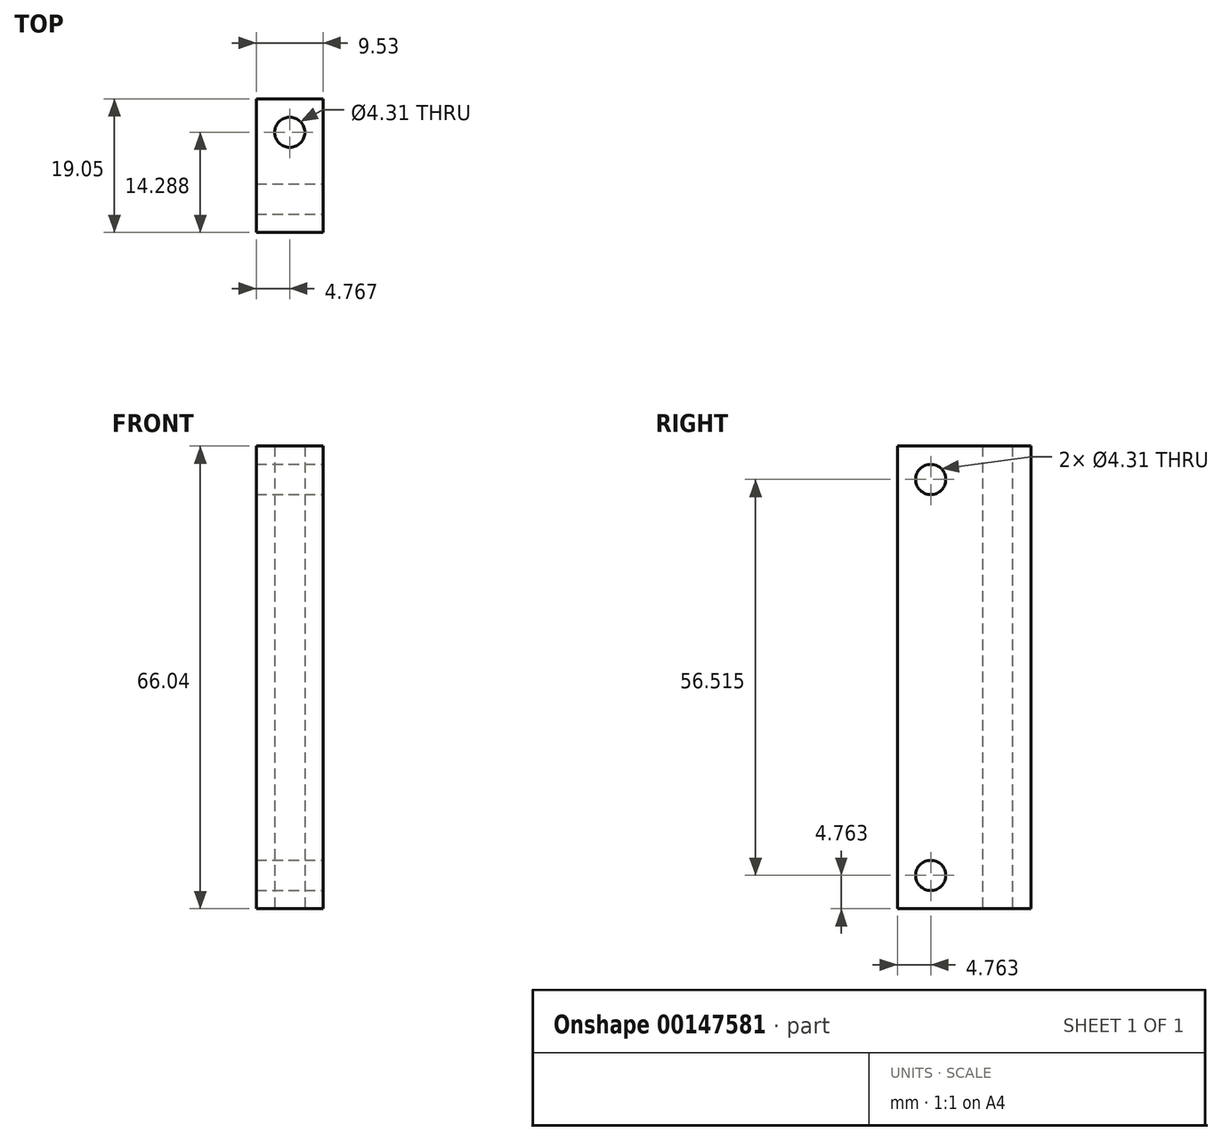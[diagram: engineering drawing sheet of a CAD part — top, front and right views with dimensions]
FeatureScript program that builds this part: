
annotation { "Feature Type Name" : "Feature", "Feature Type Description" : "" }
export const myFeature = defineFeature(function(context is Context, id is Id, definition is map)
    precondition{}
    {
        {
            var Q0;
            Q0=qCreatedBy(makeId("Top.planeOp"),FACE);
            var sketch = newSketch(context, id + "F0", { "sketchPlane" : qUnion([Q0])});
            skLineSegment(sketch, "E0.bottom", {"start": v(0, 0) * mm, "end": v(-9.53, 0) * mm});
            skLineSegment(sketch, "E0.top", {"start": v(0, -19.05) * mm, "end": v(-9.52, -19.05) * mm});
            skLineSegment(sketch, "E0.left", {"start": v(0, 0) * mm, "end": v(0, -19.05) * mm});
            skLineSegment(sketch, "E0.right", {"start": v(-9.52, 0) * mm, "end": v(-9.52, -19.05) * mm});
            skLineSegment(sketch, "E1", {"start": v(-4.76, 0) * mm, "end": v(-4.76, -4.76) * mm, "construction": true});
            skLineSegment(sketch, "E2", {"start": v(-4.76, -4.76) * mm, "end": v(0, -4.76) * mm, "construction": true});
            skCircle(sketch, "E3", {"center": v(-4.76, -4.76) * mm, "radius": 2.15 * mm});
            skSolve(sketch);
        }
        {
            var Q0;
            Q0=qSketchRegion(id+"F0",true);
            extrude(context, id + "F1", {"entities" : qUnion([Q0]), "depth" : 66.04 * mm});
        }
        {
            var Q0;
            Q0=makeQuery(id+"F1.opExtrude","SWEPT_FACE",FACE,{"disambiguationData":[OSD([sQuery(id+"F0.wireOp",EDGE,"E0.left")])]});
            var sketch = newSketch(context, id + "F2", { "sketchPlane" : qUnion([Q0])});
            skLineSegment(sketch, "E4", {"start": v(-14.29, 66.04) * mm, "end": v(-14.29, 61.28) * mm, "construction": true});
            skLineSegment(sketch, "E5", {"start": v(-14.29, 61.28) * mm, "end": v(-19.05, 61.28) * mm, "construction": true});
            skLineSegment(sketch, "E6", {"start": v(-14.29, 0) * mm, "end": v(-14.29, 4.76) * mm, "construction": true});
            skCircle(sketch, "E7", {"center": v(-14.29, 61.28) * mm, "radius": 2.15 * mm});
            skCircle(sketch, "E8", {"center": v(-14.29, 4.76) * mm, "radius": 2.15 * mm});
            skSolve(sketch);
        }
        {
            var Q0;
            Q0=qSketchRegion(id+"F2",true);
            var Q1;
            Q1=makeQuery(id+"F1.opExtrude","SWEPT_FACE",FACE,{"disambiguationData":[OSD([sQuery(id+"F0.wireOp",EDGE,"E0.right")])]});
            extrude(context, id + "F3", {"entities" : qUnion([Q0]), "operationType" : NewBodyOperationType.REMOVE, "endBound" : BoundingType.UP_TO_SURFACE, "oppositeDirection" : true, "endBoundEntityFace" : qUnion([Q1]), "depth" : 25.4 * mm});
        }
    });
